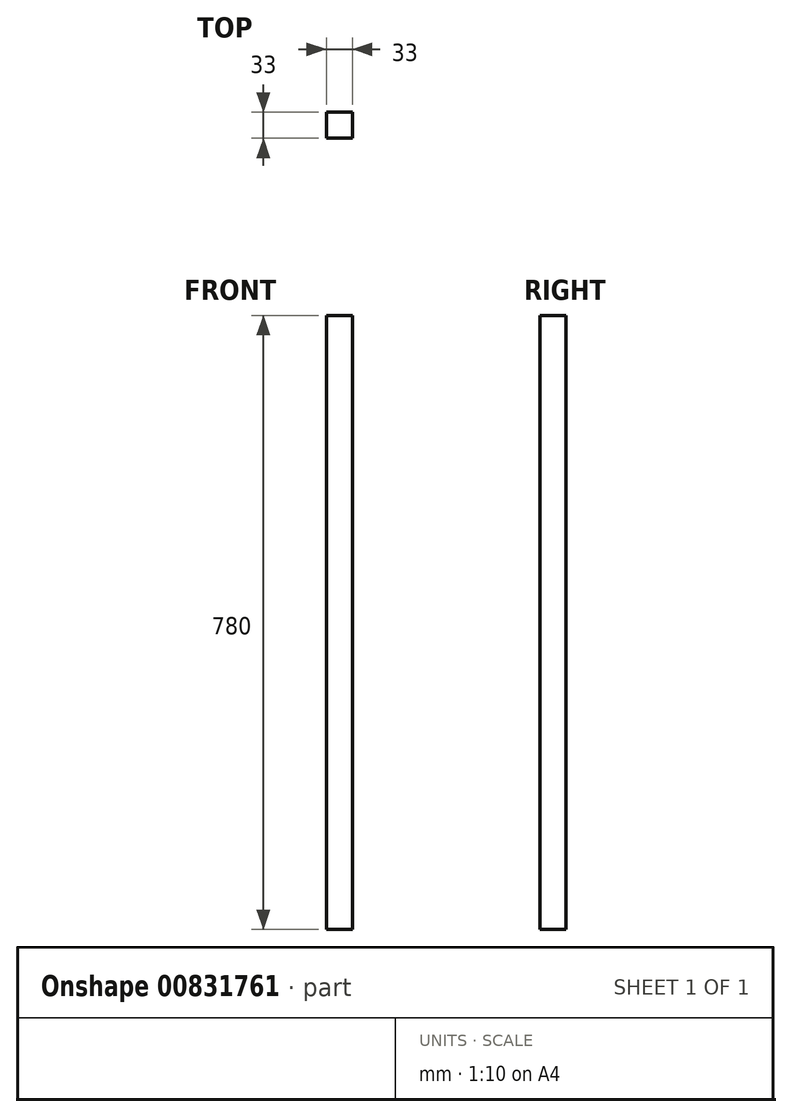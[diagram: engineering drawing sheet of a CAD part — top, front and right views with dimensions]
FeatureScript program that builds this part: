
annotation { "Feature Type Name" : "Feature", "Feature Type Description" : "" }
export const myFeature = defineFeature(function(context is Context, id is Id, definition is map)
    precondition{}
    {
        {
            var Q0;
            Q0=qCreatedBy(makeId("Top.planeOp"),FACE);
            var sketch = newSketch(context, id + "F0", { "sketchPlane" : qUnion([Q0])});
            skLineSegment(sketch, "E0.bottom", {"start": v(-105.99, 10.18) * mm, "end": v(-72.99, 10.18) * mm});
            skLineSegment(sketch, "E0.top", {"start": v(-105.99, -22.82) * mm, "end": v(-72.99, -22.82) * mm});
            skLineSegment(sketch, "E0.left", {"start": v(-105.99, 10.18) * mm, "end": v(-105.99, -22.82) * mm});
            skLineSegment(sketch, "E0.right", {"start": v(-72.99, 10.18) * mm, "end": v(-72.99, -22.82) * mm});
            skLineSegment(sketch, "E1.bottom", {"start": v(-72.99, -6.32) * mm, "end": v(-72.99, -6.32) * mm});
            skLineSegment(sketch, "E1.top", {"start": v(-72.99, -6.32) * mm, "end": v(-72.99, -6.32) * mm});
            skLineSegment(sketch, "E1.left", {"start": v(-72.99, -6.32) * mm, "end": v(-72.99, -6.32) * mm});
            skLineSegment(sketch, "E1.right", {"start": v(-72.99, -6.32) * mm, "end": v(-72.99, -6.32) * mm});
            skSolve(sketch);
        }
        {
            var Q0;
            Q0=makeQuery(id+"F0.imprint","IMPRINT",FACE,{"disambiguationData":[TD([[makeQuery(id+"F0.imprint","IMPRINT",EDGE,{"derivedFrom":sQuery(id+"F0.wireOp",EDGE,"E0.bottom")}),-1.0]])]});
            extrude(context, id + "F1", {"entities" : qUnion([Q0]), "depth" : 780 * mm, "offsetDistance" : 25 * mm});
        }
    });
